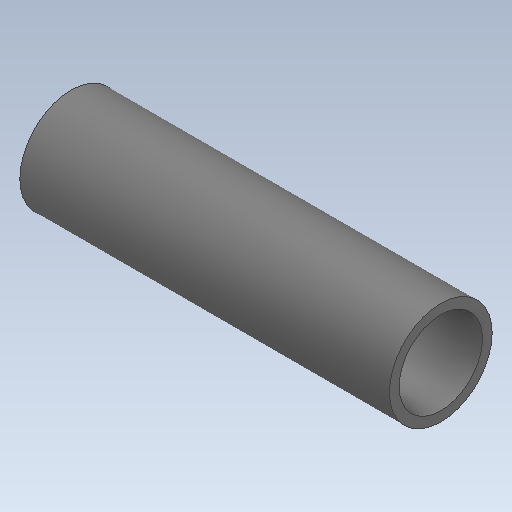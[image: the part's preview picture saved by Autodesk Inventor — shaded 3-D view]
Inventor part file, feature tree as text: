
AUTODESK INVENTOR PART (.ipt)
format: ipt  version: 2020 (Build 240168000, 168)  size: 106,496 bytes
history: native  units: in
note: dims shown in document units (in); Inventor stores cm internally (conversion verified against a paired STEP export)
features: extrude x1
ambient origin geometry x8: Origin, YZ Plane, XZ Plane, XY Plane, X Axis, Y Axis, Z Axis, Center Point
bodies: Solid1 (feature_tree)
feature tree (1):
  extrude  "Extrude-Thin1"  [1 undecoded]
note: 1 required parameter value undecoded (feature->parameter linkage not recoverable at this tier; creation-order binding heuristic only, values carry confidence <= 0.55)
